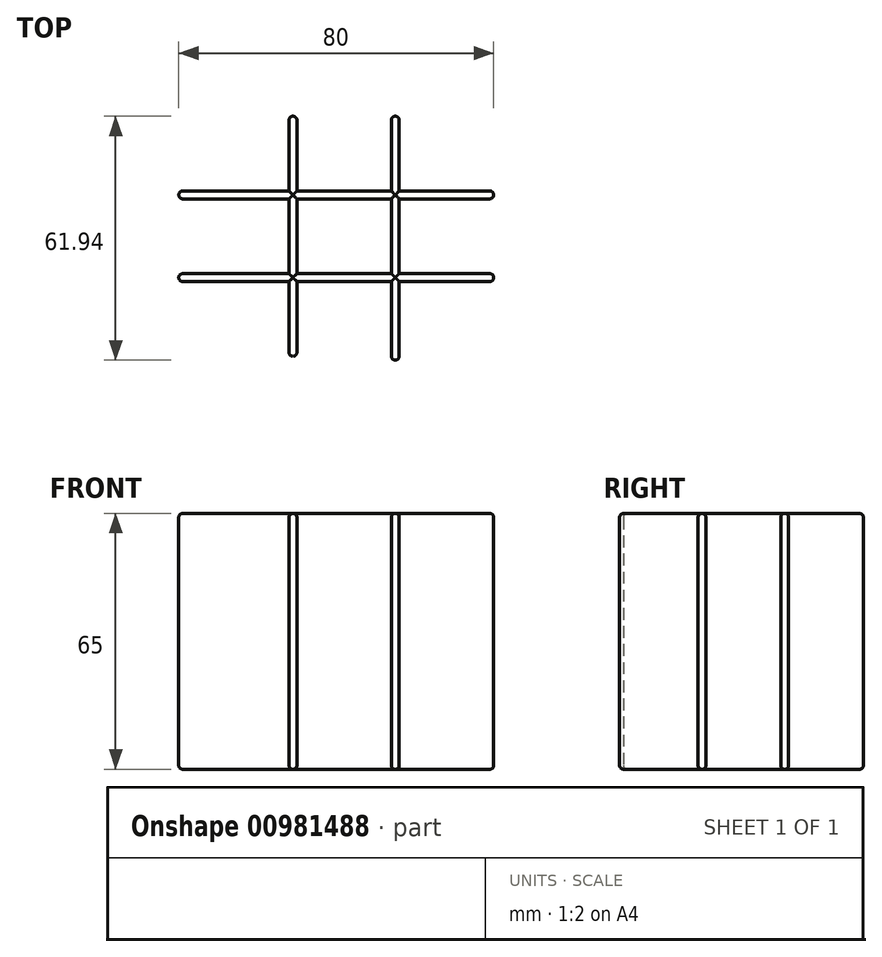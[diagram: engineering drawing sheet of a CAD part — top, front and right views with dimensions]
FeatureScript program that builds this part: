
annotation { "Feature Type Name" : "Feature", "Feature Type Description" : "" }
export const myFeature = defineFeature(function(context is Context, id is Id, definition is map)
    precondition{}
    {
        {
            var Q0;
            Q0=qCreatedBy(makeId("Top.planeOp"),FACE);
            var sketch = newSketch(context, id + "F0", { "sketchPlane" : qUnion([Q0])});
            skLineSegment(sketch, "E0.bottom", {"start": v(0, 0) * mm, "end": v(80, 0) * mm});
            skLineSegment(sketch, "E0.top", {"start": v(0, 2) * mm, "end": v(80, 2) * mm});
            skLineSegment(sketch, "E0.left", {"start": v(0, 0) * mm, "end": v(0, 2) * mm});
            skLineSegment(sketch, "E0.right", {"start": v(80, 0) * mm, "end": v(80, 2) * mm});
            skLineSegment(sketch, "E1.bottom", {"start": v(0, 23) * mm, "end": v(80, 23) * mm});
            skLineSegment(sketch, "E1.top", {"start": v(0, 21) * mm, "end": v(80, 21) * mm});
            skLineSegment(sketch, "E1.left", {"start": v(0, 23) * mm, "end": v(0, 21) * mm});
            skLineSegment(sketch, "E1.right", {"start": v(80, 23) * mm, "end": v(80, 21) * mm});
            skPoint(sketch, "E2.right.end.orphan", {"position": v(80, -21) * mm});
            skLineSegment(sketch, "E3.bottom", {"start": v(28, 42) * mm, "end": v(30, 42) * mm});
            skLineSegment(sketch, "E3.top", {"start": v(28, -19) * mm, "end": v(30, -19) * mm});
            skLineSegment(sketch, "E3.left", {"start": v(28, 42) * mm, "end": v(28, -19) * mm});
            skLineSegment(sketch, "E3.right", {"start": v(30, 42) * mm, "end": v(30, -19) * mm});
            skLineSegment(sketch, "E4.bottom", {"start": v(54, 42) * mm, "end": v(56, 42) * mm});
            skLineSegment(sketch, "E4.top", {"start": v(54, -19.94) * mm, "end": v(56, -19.94) * mm});
            skLineSegment(sketch, "E4.left", {"start": v(54, 42) * mm, "end": v(54, -19.94) * mm});
            skLineSegment(sketch, "E4.right", {"start": v(56, 42) * mm, "end": v(56, -19.94) * mm});
            skSolve(sketch);
        }
        {
            var Q0;
            {var subQ5=sQuery(id+"F0.wireOp",EDGE,"E3.bottom");Q0=makeQuery(id+"F0.imprint","IMPRINT",FACE,{"disambiguationData":[TD([[makeQuery(id+"F0.imprint","IMPRINT",EDGE,{"derivedFrom":subQ5}),-1.0]])]});}
            var Q1;
            {var subQ0=sQuery(id+"F0.wireOp",EDGE,"E1.left");Q1=makeQuery(id+"F0.imprint","IMPRINT",FACE,{"disambiguationData":[TD([[makeQuery(id+"F0.imprint","IMPRINT",EDGE,{"derivedFrom":subQ0}),1.0]])]});}
            var Q2;
            {var subQ0=sQuery(id+"F0.wireOp",EDGE,"E3.right");var subQ1=sQuery(id+"F0.wireOp",EDGE,"E1.bottom");var subQ2=makeQuery(id+"F0.imprint","INTERSECT",VERTEX,{"derivedFrom":[subQ1,subQ0]});Q2=makeQuery(id+"F0.imprint","IMPRINT",FACE,{"disambiguationData":[TD([[makeQuery(id+"F0.imprint","IMPRINT",EDGE,{"disambiguationData":[TD([[subQ2,-1.0]])],"derivedFrom":subQ1}),-1.0]])]});}
            var Q3;
            {var subQ5=sQuery(id+"F0.wireOp",EDGE,"E4.bottom");Q3=makeQuery(id+"F0.imprint","IMPRINT",FACE,{"disambiguationData":[TD([[makeQuery(id+"F0.imprint","IMPRINT",EDGE,{"derivedFrom":subQ5}),-1.0]])]});}
            var Q4;
            {var subQ0=sQuery(id+"F0.wireOp",EDGE,"E4.left");var subQ1=sQuery(id+"F0.wireOp",EDGE,"E1.bottom");var subQ2=makeQuery(id+"F0.imprint","INTERSECT",VERTEX,{"derivedFrom":[subQ1,subQ0]});Q4=makeQuery(id+"F0.imprint","IMPRINT",FACE,{"disambiguationData":[TD([[makeQuery(id+"F0.imprint","IMPRINT",EDGE,{"disambiguationData":[TD([[subQ2,-1.0]])],"derivedFrom":subQ1}),-1.0]])]});}
            var Q5;
            {var subQ0=sQuery(id+"F0.wireOp",EDGE,"E1.right");Q5=makeQuery(id+"F0.imprint","IMPRINT",FACE,{"disambiguationData":[TD([[makeQuery(id+"F0.imprint","IMPRINT",EDGE,{"derivedFrom":subQ0}),-1.0]])]});}
            var Q6;
            {var subQ0=sQuery(id+"F0.wireOp",EDGE,"E0.right");Q6=makeQuery(id+"F0.imprint","IMPRINT",FACE,{"disambiguationData":[TD([[makeQuery(id+"F0.imprint","IMPRINT",EDGE,{"derivedFrom":subQ0}),1.0]])]});}
            var Q7;
            {var subQ0=sQuery(id+"F0.wireOp",EDGE,"E4.left");var subQ1=sQuery(id+"F0.wireOp",EDGE,"E0.bottom");var subQ2=makeQuery(id+"F0.imprint","INTERSECT",VERTEX,{"derivedFrom":[subQ1,subQ0]});Q7=makeQuery(id+"F0.imprint","IMPRINT",FACE,{"disambiguationData":[TD([[makeQuery(id+"F0.imprint","IMPRINT",EDGE,{"disambiguationData":[TD([[subQ2,-1.0]])],"derivedFrom":subQ1}),1.0]])]});}
            var Q8;
            {var subQ0=sQuery(id+"F0.wireOp",EDGE,"E3.right");var subQ1=sQuery(id+"F0.wireOp",EDGE,"E0.bottom");var subQ2=makeQuery(id+"F0.imprint","INTERSECT",VERTEX,{"derivedFrom":[subQ1,subQ0]});Q8=makeQuery(id+"F0.imprint","IMPRINT",FACE,{"disambiguationData":[TD([[makeQuery(id+"F0.imprint","IMPRINT",EDGE,{"disambiguationData":[TD([[subQ2,-1.0]])],"derivedFrom":subQ1}),1.0]])]});}
            var Q9;
            {var subQ0=sQuery(id+"F0.wireOp",EDGE,"E0.left");Q9=makeQuery(id+"F0.imprint","IMPRINT",FACE,{"disambiguationData":[TD([[makeQuery(id+"F0.imprint","IMPRINT",EDGE,{"derivedFrom":subQ0}),-1.0]])]});}
            var Q10;
            {var subQ0=sQuery(id+"F0.wireOp",EDGE,"E3.left");var subQ1=sQuery(id+"F0.wireOp",EDGE,"E0.bottom");var subQ2=makeQuery(id+"F0.imprint","INTERSECT",VERTEX,{"derivedFrom":[subQ1,subQ0]});Q10=makeQuery(id+"F0.imprint","IMPRINT",FACE,{"disambiguationData":[TD([[makeQuery(id+"F0.imprint","IMPRINT",EDGE,{"disambiguationData":[TD([[subQ2,-1.0]])],"derivedFrom":subQ1}),1.0]])]});}
            var Q11;
            {var subQ0=sQuery(id+"F0.wireOp",EDGE,"E3.left");var subQ1=sQuery(id+"F0.wireOp",EDGE,"E0.top");var subQ2=makeQuery(id+"F0.imprint","INTERSECT",VERTEX,{"derivedFrom":[subQ1,subQ0]});Q11=makeQuery(id+"F0.imprint","IMPRINT",FACE,{"disambiguationData":[TD([[makeQuery(id+"F0.imprint","IMPRINT",EDGE,{"disambiguationData":[TD([[subQ2,-1.0]])],"derivedFrom":subQ1}),1.0]])]});}
            var Q12;
            {var subQ5=sQuery(id+"F0.wireOp",EDGE,"E3.top");Q12=makeQuery(id+"F0.imprint","IMPRINT",FACE,{"disambiguationData":[TD([[makeQuery(id+"F0.imprint","IMPRINT",EDGE,{"derivedFrom":subQ5}),1.0]])]});}
            var Q13;
            {var subQ5=sQuery(id+"F0.wireOp",EDGE,"E4.top");Q13=makeQuery(id+"F0.imprint","IMPRINT",FACE,{"disambiguationData":[TD([[makeQuery(id+"F0.imprint","IMPRINT",EDGE,{"derivedFrom":subQ5}),1.0]])]});}
            var Q14;
            {var subQ0=sQuery(id+"F0.wireOp",EDGE,"E3.left");var subQ1=sQuery(id+"F0.wireOp",EDGE,"E1.bottom");var subQ2=makeQuery(id+"F0.imprint","INTERSECT",VERTEX,{"derivedFrom":[subQ1,subQ0]});Q14=makeQuery(id+"F0.imprint","IMPRINT",FACE,{"disambiguationData":[TD([[makeQuery(id+"F0.imprint","IMPRINT",EDGE,{"disambiguationData":[TD([[subQ2,-1.0]])],"derivedFrom":subQ1}),-1.0]])]});}
            var Q15;
            {var subQ0=sQuery(id+"F0.wireOp",EDGE,"E4.right");var subQ1=sQuery(id+"F0.wireOp",EDGE,"E0.top");var subQ2=makeQuery(id+"F0.imprint","INTERSECT",VERTEX,{"derivedFrom":[subQ1,subQ0]});Q15=makeQuery(id+"F0.imprint","IMPRINT",FACE,{"disambiguationData":[TD([[makeQuery(id+"F0.imprint","IMPRINT",EDGE,{"disambiguationData":[TD([[subQ2,1.0]])],"derivedFrom":subQ1}),1.0]])]});}
            extrude(context, id + "F1", {"entities" : qUnion([Q0, Q1, Q2, Q3, Q4, Q5, Q6, Q7, Q8, Q9, Q10, Q11, Q12, Q13, Q14, Q15]), "depth" : 65 * mm, "offsetDistance" : 25 * mm});
        }
        {
            var Q0;
            Q0=makeQuery(id+"F1.opExtrude","CAP_FACE",FACE,{"disambiguationData":[OSD([sQuery(id+"F0.wireOp",EDGE,"E0.bottom"),sQuery(id+"F0.wireOp",EDGE,"E0.top"),sQuery(id+"F0.wireOp",EDGE,"E0.left"),sQuery(id+"F0.wireOp",EDGE,"E0.right"),sQuery(id+"F0.wireOp",EDGE,"E1.bottom"),sQuery(id+"F0.wireOp",EDGE,"E1.top"),sQuery(id+"F0.wireOp",EDGE,"E1.left"),sQuery(id+"F0.wireOp",EDGE,"E1.right"),sQuery(id+"F0.wireOp",EDGE,"E3.bottom"),sQuery(id+"F0.wireOp",EDGE,"E3.top"),sQuery(id+"F0.wireOp",EDGE,"E3.left"),sQuery(id+"F0.wireOp",EDGE,"E3.right"),sQuery(id+"F0.wireOp",EDGE,"E4.bottom"),sQuery(id+"F0.wireOp",EDGE,"E4.top"),sQuery(id+"F0.wireOp",EDGE,"E4.left"),sQuery(id+"F0.wireOp",EDGE,"E4.right")])],"isStart":false});
            var Q1;
            Q1=makeQuery(id+"F1.opExtrude","CAP_FACE",FACE,{"disambiguationData":[OSD([sQuery(id+"F0.wireOp",EDGE,"E0.bottom"),sQuery(id+"F0.wireOp",EDGE,"E0.top"),sQuery(id+"F0.wireOp",EDGE,"E0.left"),sQuery(id+"F0.wireOp",EDGE,"E0.right"),sQuery(id+"F0.wireOp",EDGE,"E1.bottom"),sQuery(id+"F0.wireOp",EDGE,"E1.top"),sQuery(id+"F0.wireOp",EDGE,"E1.left"),sQuery(id+"F0.wireOp",EDGE,"E1.right"),sQuery(id+"F0.wireOp",EDGE,"E3.bottom"),sQuery(id+"F0.wireOp",EDGE,"E3.top"),sQuery(id+"F0.wireOp",EDGE,"E3.left"),sQuery(id+"F0.wireOp",EDGE,"E3.right"),sQuery(id+"F0.wireOp",EDGE,"E4.bottom"),sQuery(id+"F0.wireOp",EDGE,"E4.top"),sQuery(id+"F0.wireOp",EDGE,"E4.left"),sQuery(id+"F0.wireOp",EDGE,"E4.right")])],"isStart":true});
            var Q2;
            Q2=makeQuery(id+"F1.opExtrude","SWEPT_FACE",FACE,{"disambiguationData":[OSD([sQuery(id+"F0.wireOp",EDGE,"E3.bottom")])]});
            var Q3;
            Q3=makeQuery(id+"F1.opExtrude","SWEPT_FACE",FACE,{"disambiguationData":[OSD([sQuery(id+"F0.wireOp",EDGE,"E4.bottom")])]});
            var Q4;
            Q4=makeQuery(id+"F1.opExtrude","SWEPT_FACE",FACE,{"disambiguationData":[OSD([sQuery(id+"F0.wireOp",EDGE,"E1.left")])]});
            var Q5;
            Q5=makeQuery(id+"F1.opExtrude","SWEPT_FACE",FACE,{"disambiguationData":[OSD([sQuery(id+"F0.wireOp",EDGE,"E0.left")])]});
            var Q6;
            Q6=makeQuery(id+"F1.opExtrude","SWEPT_FACE",FACE,{"disambiguationData":[OSD([sQuery(id+"F0.wireOp",EDGE,"E3.top")])]});
            var Q7;
            Q7=makeQuery(id+"F1.opExtrude","SWEPT_FACE",FACE,{"disambiguationData":[OSD([sQuery(id+"F0.wireOp",EDGE,"E4.top")])]});
            var Q8;
            Q8=makeQuery(id+"F1.opExtrude","SWEPT_FACE",FACE,{"disambiguationData":[OSD([sQuery(id+"F0.wireOp",EDGE,"E0.right")])]});
            var Q9;
            Q9=makeQuery(id+"F1.opExtrude","SWEPT_FACE",FACE,{"disambiguationData":[OSD([sQuery(id+"F0.wireOp",EDGE,"E1.right")])]});
            fillet(context, id + "F2", {"entities" : qUnion([Q0, Q1, Q2, Q3, Q4, Q5, Q6, Q7, Q8, Q9]), "radius" : 1 * mm, "tangentPropagation" : true, "allowEdgeOverflow" : false});
        }
    });
